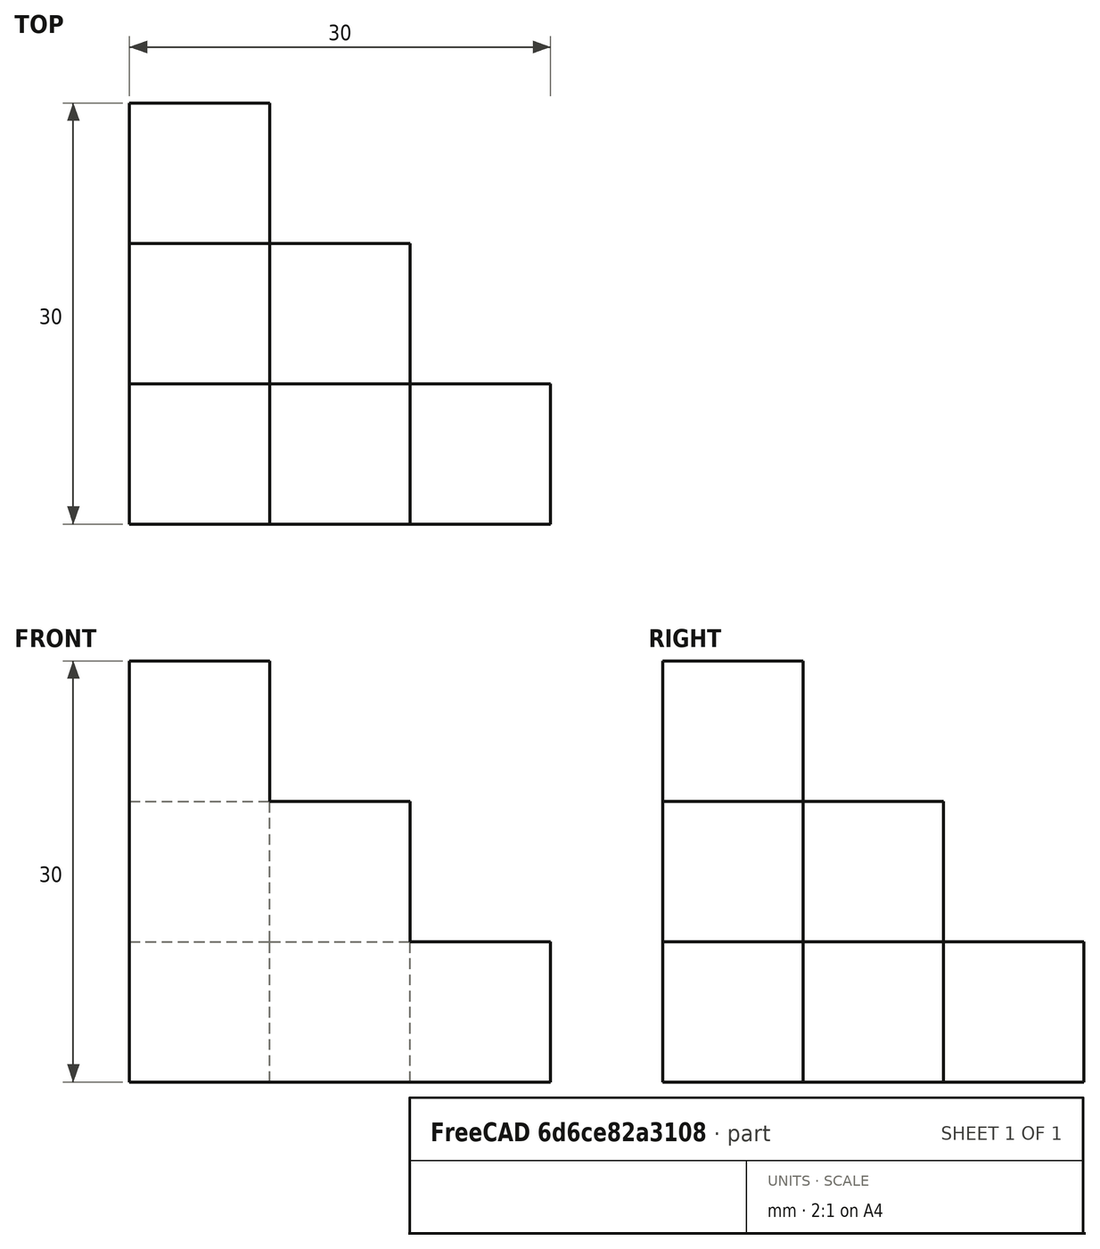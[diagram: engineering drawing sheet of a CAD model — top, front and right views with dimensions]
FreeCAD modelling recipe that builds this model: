
FCSTD DOCUMENT  (FreeCAD 1.0R39319 (Git))
Label: ojt1_t05r02_refineQbert_3-levels
License: All rights reserved
LicenseURL: https://en.wikipedia.org/wiki/All_rights_reserved
objects: Part::Box×6, Part::MultiFuse×1
note: 7 computed .brp shape members not serialized (recipe doc carries the construction recipe); baked Part::Feature solids carry a one-line shape summary decoded from their .brp

FEATURE [Part::Box] Box  label="Cub"
  AttacherType = Attacher::AttachEngine3D
  Height = 30
  Length = 10
  Width = 10
FEATURE [Part::Box] Box001  label="Cub001"
  AttacherType = Attacher::AttachEngine3D
  Height = 10
  Length = 20
  Placement = pos=(10,0,0) rot=(0,0,1;0rad)
  Width = 10
FEATURE [Part::Box] Box002  label="Cub002"
  AttacherType = Attacher::AttachEngine3D
  Height = 10
  Length = 10
  Placement = pos=(10,0,10) rot=(0,0,1;0rad)
  Width = 10
FEATURE [Part::Box] Box003  label="Cub003"
  AttacherType = Attacher::AttachEngine3D
  Height = 10
  Length = 10
  Placement = pos=(0,10,10) rot=(0,0,1;0rad)
  Width = 10
FEATURE [Part::Box] Box004  label="Cub004"
  AttacherType = Attacher::AttachEngine3D
  Height = 10
  Length = 10
  Placement = pos=(0,10,0) rot=(0.2,0,1.2;0rad)
  Width = 20
FEATURE [Part::Box] Box005  label="Cub005"
  AttacherType = Attacher::AttachEngine3D
  Height = 10
  Length = 10
  Placement = pos=(10,10,0) rot=(0,0,1;0rad)
  Width = 10
FEATURE [Part::MultiFuse] Fusion
  Refine = true
  Shapes = -> [Box005,Box004,Box003,Box002,Box001,Box]
